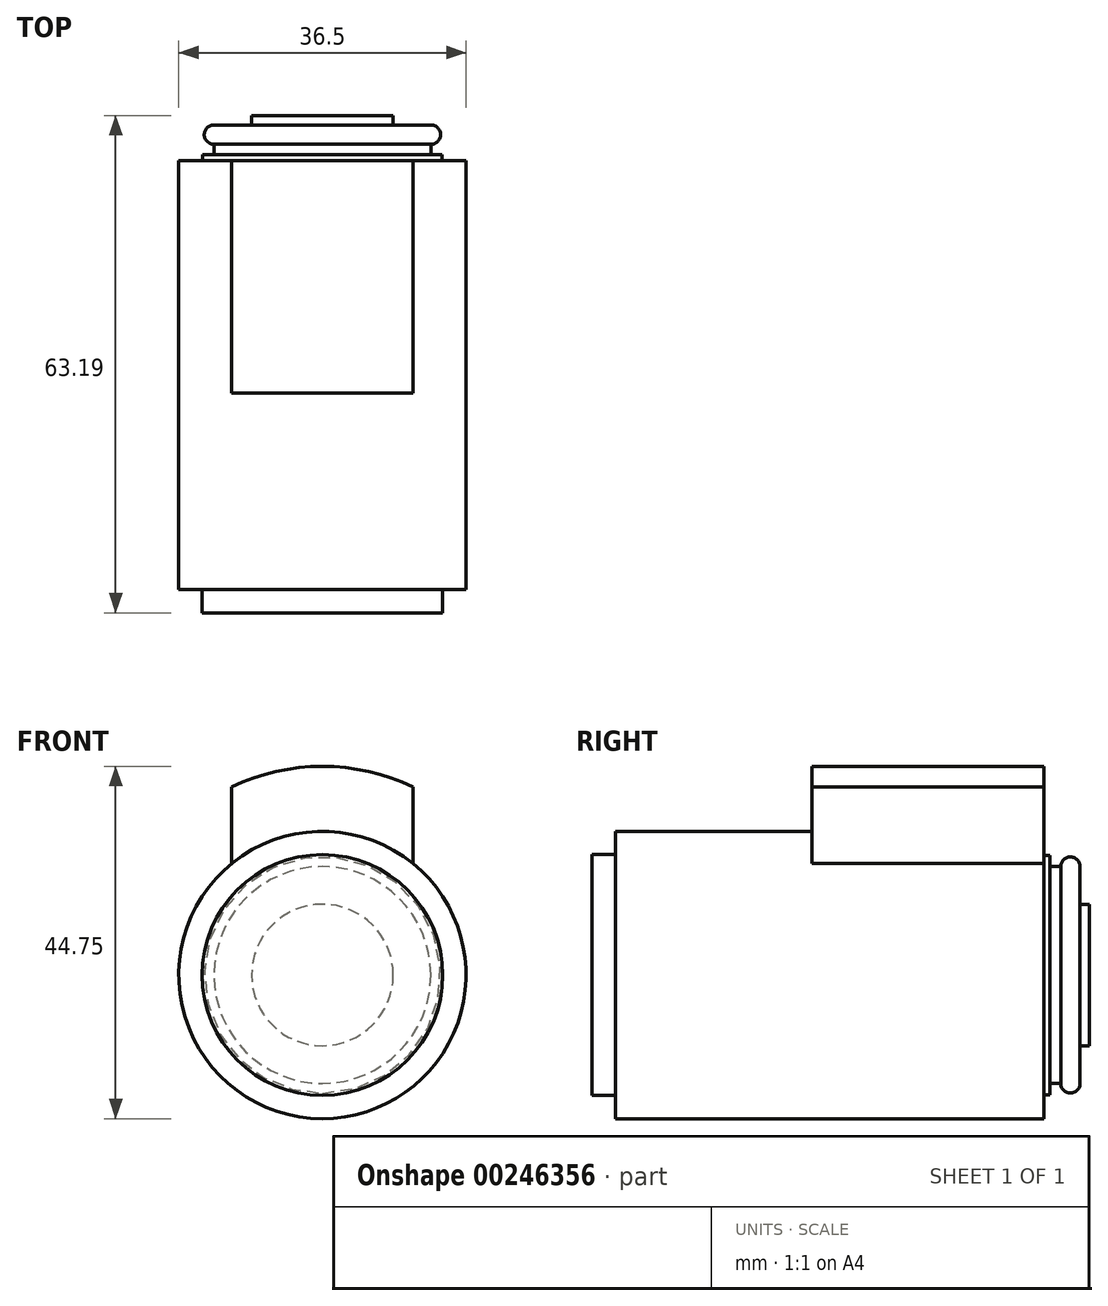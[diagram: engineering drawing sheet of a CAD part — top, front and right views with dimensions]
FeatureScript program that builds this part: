
annotation { "Feature Type Name" : "Feature", "Feature Type Description" : "" }
export const myFeature = defineFeature(function(context is Context, id is Id, definition is map)
    precondition{}
    {
        {
            var Q0;
            Q0=qCreatedBy(makeId("Front.planeOp"),FACE);
            var sketch = newSketch(context, id + "F0", { "sketchPlane" : qUnion([Q0])});
            skCircle(sketch, "E0", {"center": v(0, 0) * mm, "radius": 18.25 * mm});
            skSolve(sketch);
        }
        {
            var Q0;
            Q0=makeQuery(id+"F0.imprint","IMPRINT",FACE,{"disambiguationData":[TD([[makeQuery(id+"F0.imprint","IMPRINT",EDGE,{"derivedFrom":sQuery(id+"F0.wireOp",EDGE,"E0")}),1.0]])]});
            extrude(context, id + "F1", {"entities" : qUnion([Q0]), "depth" : 58.2 * mm});
        }
        {
            var Q0;
            Q0=makeQuery(id+"F1.opExtrude","CAP_FACE",FACE,{"disambiguationData":[OSD([sQuery(id+"F0.wireOp",EDGE,"E0")])],"isStart":true});
            var sketch = newSketch(context, id + "F2", { "sketchPlane" : qUnion([Q0])});
            skCircle(sketch, "E1", {"center": v(0, 0) * mm, "radius": 15.2 * mm});
            skCircle(sketch, "E2", {"center": v(0, 0) * mm, "radius": 19.63 * mm});
            skSolve(sketch);
        }
        {
            var Q0;
            Q0=makeQuery(id+"F2.imprint","IMPRINT",FACE,{"disambiguationData":[TD([[makeQuery(id+"F2.imprint","IMPRINT",EDGE,{"derivedFrom":sQuery(id+"F2.wireOp",EDGE,"E2")}),1.0]])]});
            var Q1;
            Q1=makeQuery(id+"F2.imprint","IMPRINT",FACE,{"disambiguationData":[TD([[makeQuery(id+"F2.imprint","IMPRINT",EDGE,{"derivedFrom":sQuery(id+"F2.wireOp",EDGE,"E1")}),-1.0]])]});
            extrude(context, id + "F3", {"entities" : qUnion([Q0, Q1]), "operationType" : NewBodyOperationType.REMOVE, "oppositeDirection" : true, "depth" : 0.76 * mm});
        }
        {
            var Q0;
            Q0=makeQuery(id+"F3.boolean.opBoolean","COPY",FACE,{"derivedFrom":makeQuery(id+"F3.opExtrude","CAP_FACE",FACE,{"disambiguationData":[OSD([sQuery(id+"F2.wireOp",EDGE,"E1"),sQuery(id+"F2.wireOp",EDGE,"E2")])],"isStart":false})});
            var sketch = newSketch(context, id + "F4", { "sketchPlane" : qUnion([Q0])});
            skLineSegment(sketch, "E3", {"start": v(-11.5, 14.17) * mm, "end": v(-11.5, 23.88) * mm});
            skLineSegment(sketch, "E4", {"start": v(11.5, 23.88) * mm, "end": v(11.5, 14.17) * mm});
            skArc(sketch, "E5", {"start": v(11.5, 14.17) * mm, "mid": v(0, 18.25) * mm, "end": v(-11.5, 14.17) * mm});
            skLineSegment(sketch, "E6", {"start": v(0, 35.34) * mm, "end": v(0, -22.32) * mm, "construction": true});
            skArc(sketch, "E7", {"start": v(11.5, 23.88) * mm, "mid": v(0, 26.5) * mm, "end": v(-11.5, 23.88) * mm});
            skPoint(sketch, "E8.orphan", {"position": v(-11.5, 27.8) * mm});
            skPoint(sketch, "E9.orphan", {"position": v(11.5, 27.8) * mm});
            skSolve(sketch);
        }
        {
            var Q0;
            Q0=makeQuery(id+"F4.imprint","IMPRINT",FACE,{"disambiguationData":[TD([[makeQuery(id+"F4.imprint","IMPRINT",EDGE,{"derivedFrom":sQuery(id+"F4.wireOp",EDGE,"E3")}),-1.0]])]});
            extrude(context, id + "F5", {"entities" : qUnion([Q0]), "operationType" : NewBodyOperationType.ADD, "oppositeDirection" : true, "depth" : 29.5 * mm});
        }
        {
            var Q0;
            Q0=qCreatedBy(makeId("Right.planeOp"),FACE);
            var sketch = newSketch(context, id + "F6", { "sketchPlane" : qUnion([Q0])});
            skLineSegment(sketch, "E10.0", {"start": v(5, 9) * mm, "end": v(5, 0) * mm});
            skLineSegment(sketch, "E11", {"start": v(0, 13.77) * mm, "end": v(1.34, 13.77) * mm});
            skArc(sketch, "E12", {"start": v(3.8, 13.77) * mm, "mid": v(2.57, 15) * mm, "end": v(1.34, 13.77) * mm});
            skLineSegment(sketch, "E13", {"start": v(3.8, 13.77) * mm, "end": v(3.8, 9) * mm});
            skLineSegment(sketch, "E14", {"start": v(3.8, 9) * mm, "end": v(5, 9) * mm});
            skLineSegment(sketch, "E15", {"start": v(-13.68, 0) * mm, "end": v(13.85, 0) * mm, "construction": true});
            skLineSegment(sketch, "E16", {"start": v(0, 13.77) * mm, "end": v(0, 0) * mm});
            skLineSegment(sketch, "E17", {"start": v(0, 0) * mm, "end": v(5, 0) * mm});
            skSolve(sketch);
        }
        {
            var Q0;
            Q0=makeQuery(id+"F6.imprint","IMPRINT",FACE,{"disambiguationData":[TD([[makeQuery(id+"F6.imprint","IMPRINT",EDGE,{"derivedFrom":sQuery(id+"F6.wireOp",EDGE,"E10.0")}),-1.0]])]});
            var Q1;
            Q1=sQuery(id+"F6.wireOp",EDGE,"E15");
            revolve(context, id + "F7", {"operationType" : NewBodyOperationType.ADD, "entities" : qUnion([Q0]), "axis" : qUnion([Q1]), "revolveType" : RevolveType.FULL});
        }
        {
            var Q0;
            Q0=makeQuery(id+"F1.opExtrude","CAP_FACE",FACE,{"disambiguationData":[OSD([sQuery(id+"F0.wireOp",EDGE,"E0")])],"isStart":false});
            var sketch = newSketch(context, id + "F8", { "sketchPlane" : qUnion([Q0])});
            skCircle(sketch, "E18", {"center": v(0, 0) * mm, "radius": 15.29 * mm});
            skCircle(sketch, "E19", {"center": v(0, 0) * mm, "radius": 19.98 * mm});
            skSolve(sketch);
        }
        {
            var Q0;
            Q0=makeQuery(id+"F8.imprint","IMPRINT",FACE,{"disambiguationData":[TD([[makeQuery(id+"F8.imprint","IMPRINT",EDGE,{"derivedFrom":sQuery(id+"F8.wireOp",EDGE,"E19")}),1.0]])]});
            var Q1;
            Q1=makeQuery(id+"F8.imprint","IMPRINT",FACE,{"disambiguationData":[TD([[makeQuery(id+"F8.imprint","IMPRINT",EDGE,{"derivedFrom":sQuery(id+"F8.wireOp",EDGE,"E18")}),-1.0]])]});
            extrude(context, id + "F9", {"entities" : qUnion([Q0, Q1]), "operationType" : NewBodyOperationType.REMOVE, "oppositeDirection" : true, "depth" : 3 * mm});
        }
    });
